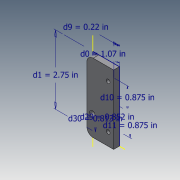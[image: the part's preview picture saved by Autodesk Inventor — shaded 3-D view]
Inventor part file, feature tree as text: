
AUTODESK INVENTOR PART (.ipt)
format: ipt  version: 2018.3 (Build 223284000, 284)  size: 114,688 bytes
history: native  units: in
note: dims shown in document units (in); Inventor stores cm internally (conversion verified against a paired STEP export)
features: hole x2, sketch x1, extrude x1, fillet x1
ambient origin geometry x8: Origin, YZ Plane, XZ Plane, XY Plane, X Axis, Y Axis, Z Axis, Center Point
bodies: Solid1 (feature_tree)
feature tree (5):
  sketch  "Sketch1"  dims[d0=1.07in d1=2.75in d9=0.22in d10=0.875in d11=0.875in d12=0.23in d13=0.0in d14=0.15in d15=0.75in d16=0.375in d17=0.25in d18=0.5635in d19=1.0in d20=0.8108in d21=0.211in d22=0.75in d23=0.375in d24=0.25in d25=0.5635in d26=1.0in d27=0.8108in d28=0.25in d29=0.852in d30=0.813in]
  extrude  "Extrusion1"  Depth=2.75in
  hole  "Hole1"  [1 undecoded]
  hole  "Hole2"  [1 undecoded]
  fillet  "Fillet1"  Radius=0.875in
note: 2 required parameter values undecoded (feature->parameter linkage not recoverable at this tier; creation-order binding heuristic only, values carry confidence <= 0.55)
